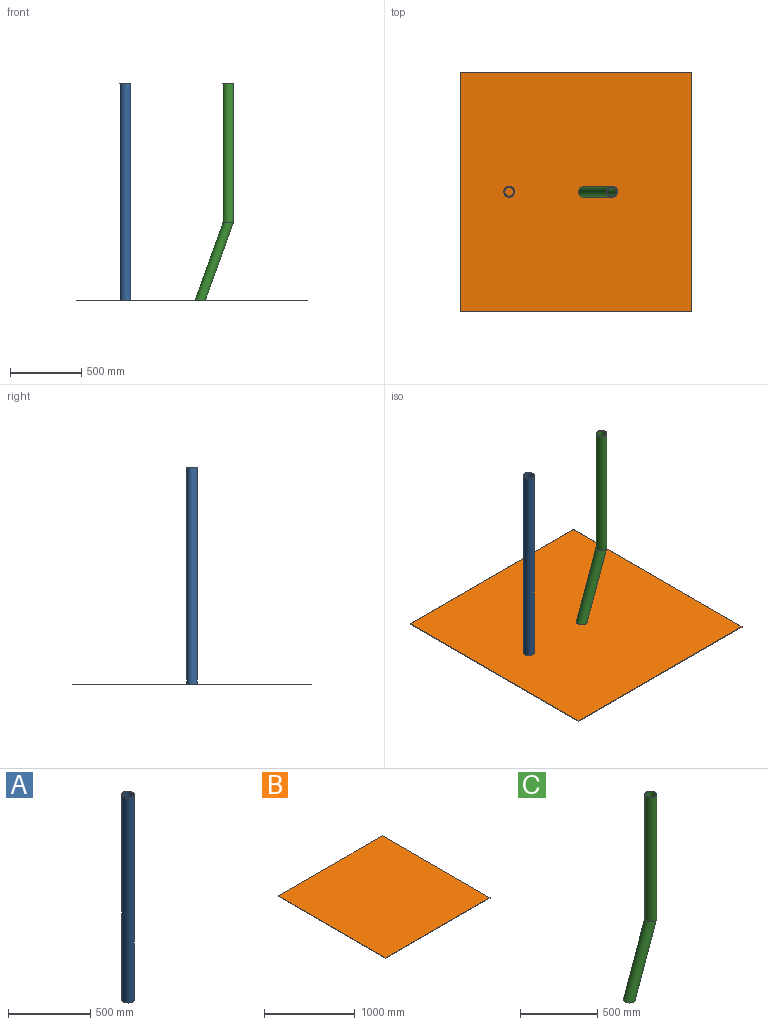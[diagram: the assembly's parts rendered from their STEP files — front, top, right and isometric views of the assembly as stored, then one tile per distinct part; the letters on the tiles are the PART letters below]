
ASSEMBLY  parts=3 mates=2
PART A: 4 faces, bbox 76.2x76.2x1524 mm
  f0: cylinder r=31.75mm len=1524mm, axis (0,0,-1), area 304024.5mm2, adj f2,f3
  f1: cylinder r=38.1mm len=1524mm, axis (0,0,-1), area 364829.4mm2, adj f2,f3
  f2: plane 76.2x76.2mm, normal (0,0,1), area 1393.4mm2, adj f0,f1
  f3: plane 76.2x76.2mm, normal (0,0,-1), area 1393.4mm2, adj f0,f1
PART B: 6 faces, bbox 1625.6x1676.4x4.8 mm
  f0: plane 1625.6x4.76mm, normal (0,-1,0), area 7741.9mm2, adj f1,f3,f4,f5
  f1: plane 1676.4x4.76mm, normal (1,0,0), area 7983.9mm2, adj f0,f2,f4,f5
  f2: plane 1625.6x4.76mm, normal (0,1,0), area 7741.9mm2, adj f1,f3,f4,f5
  f3: plane 1676.4x4.76mm, normal (-1,0,0), area 7983.9mm2, adj f0,f2,f4,f5
  f4: plane 1676.4x1625.6mm, normal (0,0,1), area 2725155.8mm2, adj f0,f1,f2,f3
  f5: plane 1676.4x1625.6mm, normal (0,0,-1), area 2725155.8mm2, adj f0,f1,f2,f3
PART C: 6 faces, bbox 272.3x152.4x1524 mm
  f0: cylinder r=31.75mm len=980.44mm, axis (0,0,1), area 195589.1mm2, adj f1,f2
  f1: bspline ~543.56x259.59mm, area 112104.7mm2, adj f0,f3
  f2: plane 76.2x76.2mm, normal (0,0,1), area 1393.4mm2, adj f0,f4
  f3: plane 76.2x76.2mm, normal (0,0,-1), area 1393.4mm2, adj f1,f5
  f4: cylinder r=38.1mm len=980.44mm, axis (0,0,1), area 234706.9mm2, adj f2,f5
  f5: bspline ~543.56x272.29mm, area 134525.6mm2, adj f3,f4
PLACE A t=(-88.9,0,0)mm
PLACE B at identity
PLACE C t=(-349.25,0,0)mm
MATE fastened C.f3 <-> B.f4  axis (0,0,-1) through (57.15,0,4.76)mm
MATE fastened A.f0 <-> B.f4  axis (0,0,-1) through (-469.9,0,4.76)mm
